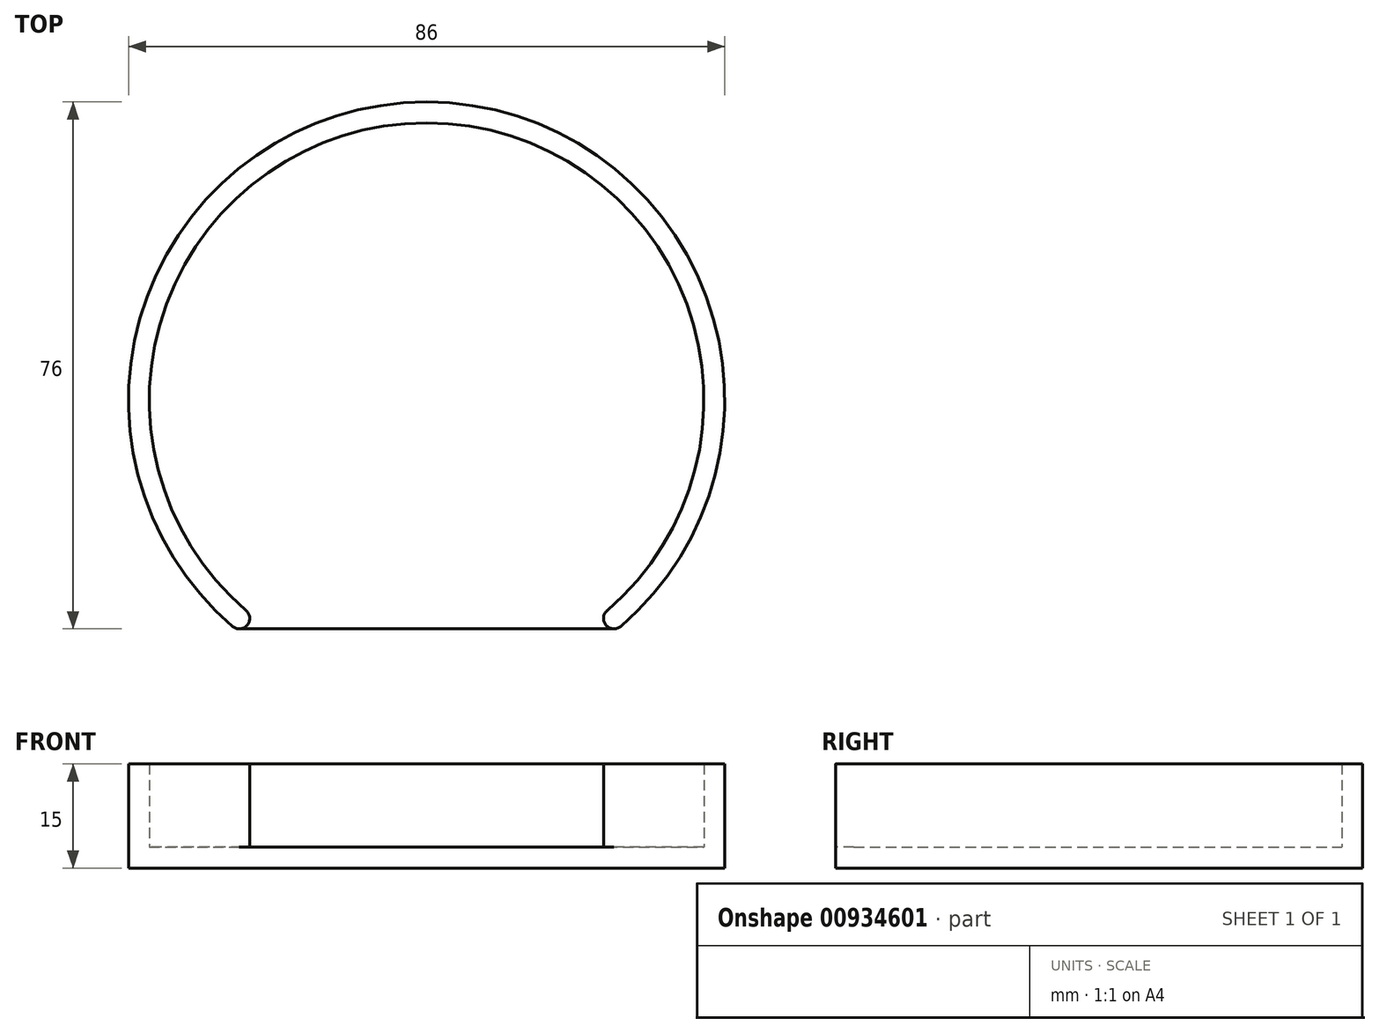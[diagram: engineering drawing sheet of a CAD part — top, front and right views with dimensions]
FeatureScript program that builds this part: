
annotation { "Feature Type Name" : "Feature", "Feature Type Description" : "" }
export const myFeature = defineFeature(function(context is Context, id is Id, definition is map)
    precondition{}
    {
        {
            var Q0;
            Q0=qCreatedBy(makeId("Top.planeOp"),FACE);
            var sketch = newSketch(context, id + "F0", { "sketchPlane" : qUnion([Q0])});
            skCircle(sketch, "E0", {"center": v(0, 0) * mm, "radius": 40 * mm});
            skCircle(sketch, "E1.0", {"center": v(0, 0) * mm, "radius": 43 * mm});
            skLineSegment(sketch, "E2", {"start": v(-27.57, -33) * mm, "end": v(27.57, -33) * mm});
            skSolve(sketch);
        }
        {
            var Q0;
            {var subQ0=sQuery(id+"F0.wireOp",EDGE,"E2");var subQ1=sQuery(id+"F0.wireOp",EDGE,"E0");var subQ2=makeQuery(id+"F0.imprint","INTERSECT",VERTEX,{"disambiguationData":[OD(0.0)],"derivedFrom":[subQ1,subQ0]});Q0=makeQuery(id+"F0.imprint","IMPRINT",FACE,{"disambiguationData":[TD([[makeQuery(id+"F0.imprint","IMPRINT",EDGE,{"disambiguationData":[TD([[subQ2,1.0]])],"derivedFrom":subQ1}),-1.0]])]});}
            extrude(context, id + "F1", {"entities" : qUnion([Q0]), "depth" : 15 * mm, "offsetDistance" : 25 * mm});
        }
        {
            var Q0;
            {var subQ0=sQuery(id+"F0.wireOp",EDGE,"E2");var subQ1=sQuery(id+"F0.wireOp",EDGE,"E0");var subQ2=makeQuery(id+"F0.imprint","INTERSECT",VERTEX,{"disambiguationData":[OD(0.0)],"derivedFrom":[subQ1,subQ0]});Q0=makeQuery(id+"F0.imprint","IMPRINT",FACE,{"disambiguationData":[TD([[makeQuery(id+"F0.imprint","IMPRINT",EDGE,{"disambiguationData":[TD([[subQ2,1.0]])],"derivedFrom":subQ1}),1.0]])]});}
            extrude(context, id + "F2", {"entities" : qUnion([Q0]), "operationType" : NewBodyOperationType.ADD, "depth" : 3 * mm, "offsetDistance" : 25 * mm});
        }
        {
            var Q0;
            {var subQ0=sQuery(id+"F0.wireOp",EDGE,"E2");var subQ1=sQuery(id+"F0.wireOp",EDGE,"E0");Q0=makeQuery(id+"F1.opExtrude","SWEPT_EDGE",EDGE,{"disambiguationData":[OSD([subQ1,subQ0]),TDD([makeQuery(id+"F0.imprint","INTERSECT",VERTEX,{"disambiguationData":[OD(0.0)],"derivedFrom":[subQ1,subQ0]})])]});}
            var Q1;
            {var subQ0=sQuery(id+"F0.wireOp",EDGE,"E2");var subQ1=sQuery(id+"F0.wireOp",EDGE,"E0");Q1=makeQuery(id+"F1.opExtrude","SWEPT_EDGE",EDGE,{"disambiguationData":[OSD([subQ1,subQ0]),TDD([makeQuery(id+"F0.imprint","INTERSECT",VERTEX,{"disambiguationData":[OD(1.0)],"derivedFrom":[subQ1,subQ0]})])]});}
            var Q2;
            {var subQ0=sQuery(id+"F0.wireOp",EDGE,"E2");var subQ1=sQuery(id+"F0.wireOp",EDGE,"E1.0");Q2=makeQuery(id+"F1.opExtrude","SWEPT_EDGE",EDGE,{"disambiguationData":[OSD([subQ1,subQ0]),TDD([makeQuery(id+"F0.imprint","INTERSECT",VERTEX,{"disambiguationData":[OD(1.0)],"derivedFrom":[subQ1,subQ0]})])]});}
            var Q3;
            {var subQ0=sQuery(id+"F0.wireOp",EDGE,"E2");var subQ1=sQuery(id+"F0.wireOp",EDGE,"E1.0");Q3=makeQuery(id+"F1.opExtrude","SWEPT_EDGE",EDGE,{"disambiguationData":[OSD([subQ1,subQ0]),TDD([makeQuery(id+"F0.imprint","INTERSECT",VERTEX,{"disambiguationData":[OD(0.0)],"derivedFrom":[subQ1,subQ0]})])]});}
            fillet(context, id + "F3", {"entities" : qUnion([Q0, Q1, Q2, Q3]), "radius" : 1.5 * mm, "tangentPropagation" : true, "allowEdgeOverflow" : false});
        }
    });
